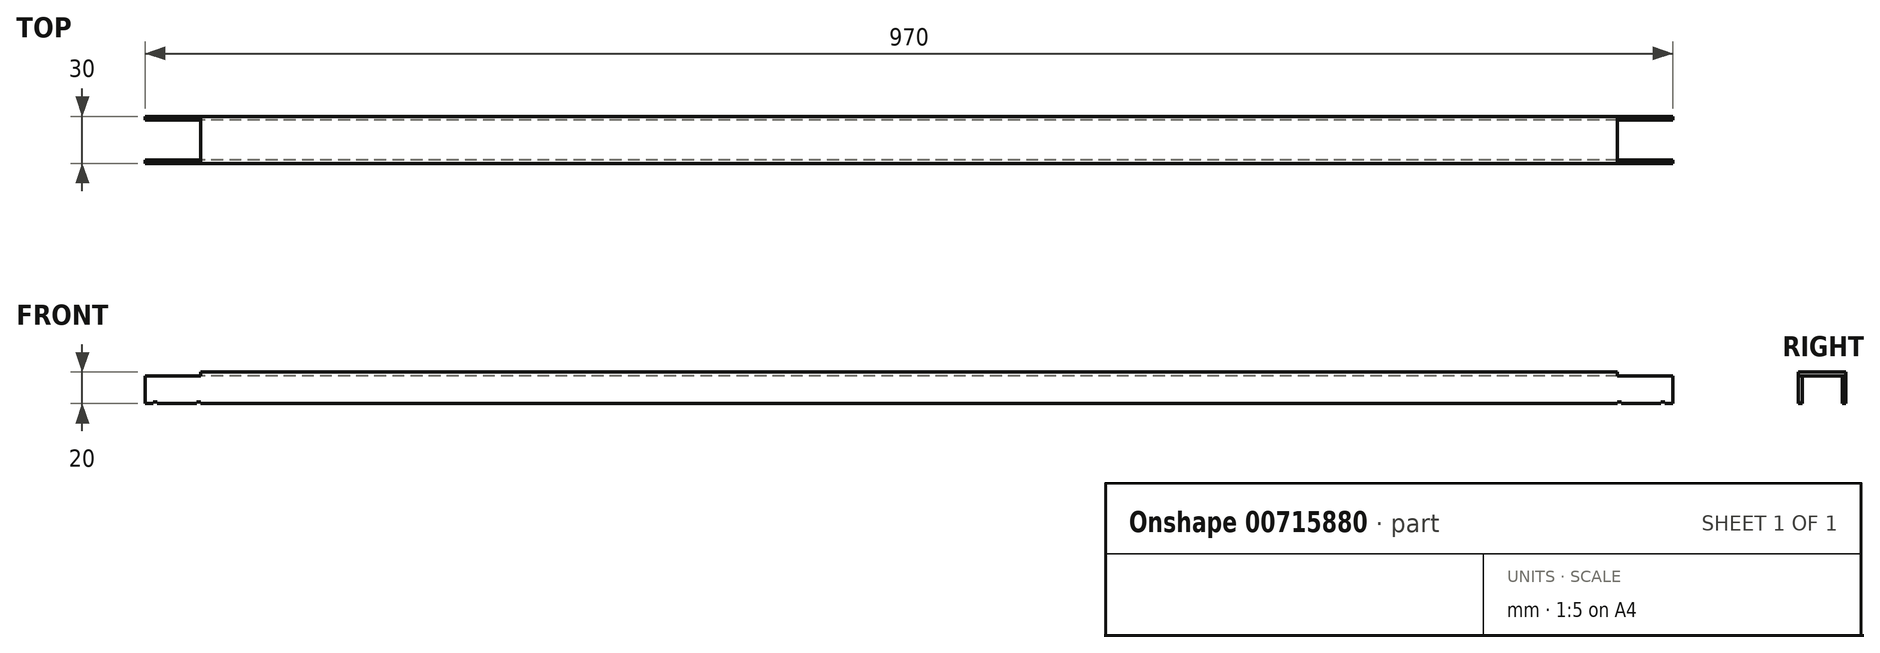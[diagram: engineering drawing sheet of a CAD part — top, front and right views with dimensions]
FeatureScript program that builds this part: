
annotation { "Feature Type Name" : "Feature", "Feature Type Description" : "" }
export const myFeature = defineFeature(function(context is Context, id is Id, definition is map)
    precondition{}
    {
        {
            var Q0;
            Q0=qCreatedBy(makeId("Right.planeOp"),FACE);
            var sketch = newSketch(context, id + "F0", { "sketchPlane" : qUnion([Q0])});
            skLineSegment(sketch, "E0.bottom", {"start": v(0, 0) * mm, "end": v(2.3, 0) * mm});
            skLineSegment(sketch, "E0.top", {"start": v(0, 20) * mm, "end": v(30, 20) * mm});
            skLineSegment(sketch, "E0.left", {"start": v(0, 0) * mm, "end": v(0, 20) * mm});
            skLineSegment(sketch, "E0.right", {"start": v(30, 0) * mm, "end": v(30, 20) * mm});
            skLineSegment(sketch, "E1.0", {"start": v(27.7, 0) * mm, "end": v(27.7, 17.7) * mm});
            skLineSegment(sketch, "E2.0", {"start": v(2.3, 17.7) * mm, "end": v(27.7, 17.7) * mm});
            skLineSegment(sketch, "E3.0", {"start": v(2.3, 0) * mm, "end": v(2.3, 17.7) * mm});
            skLineSegment(sketch, "E4.trimOffspring", {"start": v(27.7, 0) * mm, "end": v(30, 0) * mm});
            skSolve(sketch);
        }
        {
            var Q0;
            Q0 = qSketchRegion(id + "F0", true);
            extrude(context, id + "F1", {"entities" : qUnion([Q0]), "depth" : 970 * mm, "offsetDistance" : 25 * mm});
        }
        {
            var Q0;
            Q0=makeQuery(id+"F1.opExtrude","SWEPT_FACE",FACE,{"disambiguationData":[OSD([sQuery(id+"F0.wireOp",EDGE,"E0.top")])]});
            var sketch = newSketch(context, id + "F2", { "sketchPlane" : qUnion([Q0])});
            skLineSegment(sketch, "E5.bottom", {"start": v(0, 0) * mm, "end": v(35, 0) * mm});
            skLineSegment(sketch, "E5.top", {"start": v(0, 30) * mm, "end": v(35, 30) * mm});
            skLineSegment(sketch, "E5.left", {"start": v(0, 0) * mm, "end": v(0, 30) * mm});
            skLineSegment(sketch, "E5.right", {"start": v(35, 0) * mm, "end": v(35, 30) * mm});
            skLineSegment(sketch, "E6.bottom", {"start": v(970, 0) * mm, "end": v(935, 0) * mm});
            skLineSegment(sketch, "E6.top", {"start": v(970, 30) * mm, "end": v(935, 30) * mm});
            skLineSegment(sketch, "E6.left", {"start": v(970, 0) * mm, "end": v(970, 30) * mm});
            skLineSegment(sketch, "E6.right", {"start": v(935, 0) * mm, "end": v(935, 30) * mm});
            skSolve(sketch);
        }
        {
            var Q0;
            Q0 = qSketchRegion(id + "F2", true);
            extrude(context, id + "F3", {"entities" : qUnion([Q0]), "operationType" : NewBodyOperationType.REMOVE, "oppositeDirection" : true, "depth" : 2.3 * mm, "offsetDistance" : 25 * mm});
        }
        {
            var Q0;
            Q0=makeQuery(id+"F1.opExtrude","SWEPT_FACE",FACE,{"disambiguationData":[OSD([sQuery(id+"F0.wireOp",EDGE,"E0.left")])]});
            var sketch = newSketch(context, id + "F4", { "sketchPlane" : qUnion([Q0])});
            skLineSegment(sketch, "E7.bottom", {"start": v(35, 0) * mm, "end": v(32.6, 0) * mm});
            skLineSegment(sketch, "E7.top", {"start": v(35, 1) * mm, "end": v(32.6, 1) * mm});
            skLineSegment(sketch, "E7.left", {"start": v(35, 0) * mm, "end": v(35, 1) * mm});
            skLineSegment(sketch, "E7.right", {"start": v(32.6, 0) * mm, "end": v(32.6, 1) * mm});
            skLineSegment(sketch, "E8.bottom", {"start": v(7.4, 0) * mm, "end": v(5, 0) * mm});
            skLineSegment(sketch, "E8.top", {"start": v(7.4, 1) * mm, "end": v(5, 1) * mm});
            skLineSegment(sketch, "E8.left", {"start": v(7.4, 0) * mm, "end": v(7.4, 1) * mm});
            skLineSegment(sketch, "E8.right", {"start": v(5, 0) * mm, "end": v(5, 1) * mm});
            skLineSegment(sketch, "E9", {"start": v(485, 128) * mm, "end": v(485, 0) * mm, "construction": true});
            skLineSegment(sketch, "E10.MirrorCS", {"start": v(937.4, 0) * mm, "end": v(937.4, 1) * mm});
            skLineSegment(sketch, "E11.MirrorCS", {"start": v(935, 1) * mm, "end": v(937.4, 1) * mm});
            skLineSegment(sketch, "E12.MirrorCS", {"start": v(935, 0) * mm, "end": v(935, 1) * mm});
            skLineSegment(sketch, "E13.MirrorCS", {"start": v(965, 0) * mm, "end": v(965, 1) * mm});
            skLineSegment(sketch, "E14.MirrorCS", {"start": v(962.6, 1) * mm, "end": v(965, 1) * mm});
            skLineSegment(sketch, "E15.MirrorCS", {"start": v(962.6, 0) * mm, "end": v(962.6, 1) * mm});
            skLineSegment(sketch, "E16.MirrorCS", {"start": v(962.6, 0) * mm, "end": v(965, 0) * mm});
            skLineSegment(sketch, "E17.MirrorCS", {"start": v(935, 0) * mm, "end": v(937.4, 0) * mm});
            skSolve(sketch);
        }
        {
            var Q0;
            Q0 = qSketchRegion(id + "F4", true);
            extrude(context, id + "F5", {"entities" : qUnion([Q0]), "operationType" : NewBodyOperationType.REMOVE, "endBound" : BoundingType.THROUGH_ALL, "oppositeDirection" : true, "depth" : 25 * mm, "offsetDistance" : 25 * mm});
        }
    });
